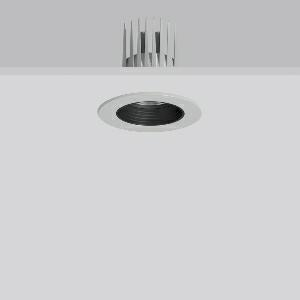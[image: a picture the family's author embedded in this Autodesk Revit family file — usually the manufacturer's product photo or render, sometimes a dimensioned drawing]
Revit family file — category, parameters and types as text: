
# Revit family: heledon_mini_e_901746_004_76_80d1
name_source: partatom
category: Lighting Fixtures
units: mm (PartAtom-declared; Revit-internal decimal feet)

## family parameters
Cut with Voids When Loaded = No
Host = Face
Light Source = No
Part Type = Normal
Room Calculation Point = No
Round Connector Dimension = Use Diameter
Shared = No

## types (1)
- HELEDON mini E (1 x LED Modul 930, 2250 lm, 3000)
    Apparent Load = 20 VA
    Approval mark = CE
    CIE Flux Codes = 80 99 100 100 100
    Color Rendering = 90
    Color Temperature = 3000
    Default Elevation = 1800 mm
    Description = Series: HELEDON mini
Round recessed downlight. Housing: die-cast aluminium, powder-coated. Black plastic ring and recessed LED to prevent glare from the side. Optical assembly with lens made of plastic (polycarbonate) for the best homogeneous light distribution - can be changed without tools. Best colour rendering index Ra>90. Suitable for Recessed ceiling mounting. Installation without tools thanks to spring fastening system. Including separate LED converter with connecting cable 600 mm.High quality converter without flickering and stroboscopic effect. Through-wiring box (5 pole) available as accessory. The following accessories can be mounted without use of tools: interchangeable lenses, decorative glasses, honeycomb louvre, clear and frosted diffusers, white interchangeable plastic ring. 
Colour: silver
Diameter: 124 mm
Height: 3 mm
Cut-out diameter: 114 mm
Recess height: 170 mm
Luminaire: recess height: 120 mm
Lamp: LED
Socket: without socket
Colour temperature: 3000K
Colour rendering index (CRI): 92
System power: 20 W
Rated luminous flux: 2250 lm
Luminous efficiency: 113 lm/W
Control gear: Converter, dimmable, DALI
Protection class: II
Type of protection: IP 20
    Height = 0 mm  [stored 0 ft]
    Lamp = 1 x LED Modul 930
    Lamp Light Flux = 2250 lm
    Lamp count = 1
    Length = 124 mm  [stored 0.406824 ft]
    Lifetime = 50000 h
    Luminous efficacy = 113 lm/W
    Manufacturer = RZB
    ModVariant = No
    Model = 901746.004.76
    Mounting Place = Ceiling
    Mounting Type = Recessed
    Number of Poles = 1
    OnlyDefault = Yes
    Power Factor = 1
    Product Name = HELEDON mini E
    Product group = Recessed downlights
    ProductGroupID = 402
    Protection Class = Protection class II
    Protection Degree = IP 20
    RLX_Detail_Level = 1
    RLX_Emergency_Light_Flux = 0 lm
    RLX_Emergency_Type = 0
    RLX_Emergency_Type_DB = No
    RlxData = <blob elided: 126369 chars, md5=077cdb17>
    Socket = socket
    Standby Power = 0 W
    System Light Flux = 2250 lm
    System Power = 20 W
    Type Comments = Product without accessories
    Type Image = 901656.004.jpg
    URL = http://relux.com
    VarID = ---
    Voltage = 230 V
    Voltage Range = 220-240 V
    Weight = 0.00 kg
    Width = 0 mm  [stored 0 ft]

note: [stored X ft] marks values corroborated as IEEE doubles in the binary element streams (Revit-internal decimal feet)

## geometry (parser evidence)
native form markers: Blend x4, Sweep x12
no freeform markers — native parametric forms only
